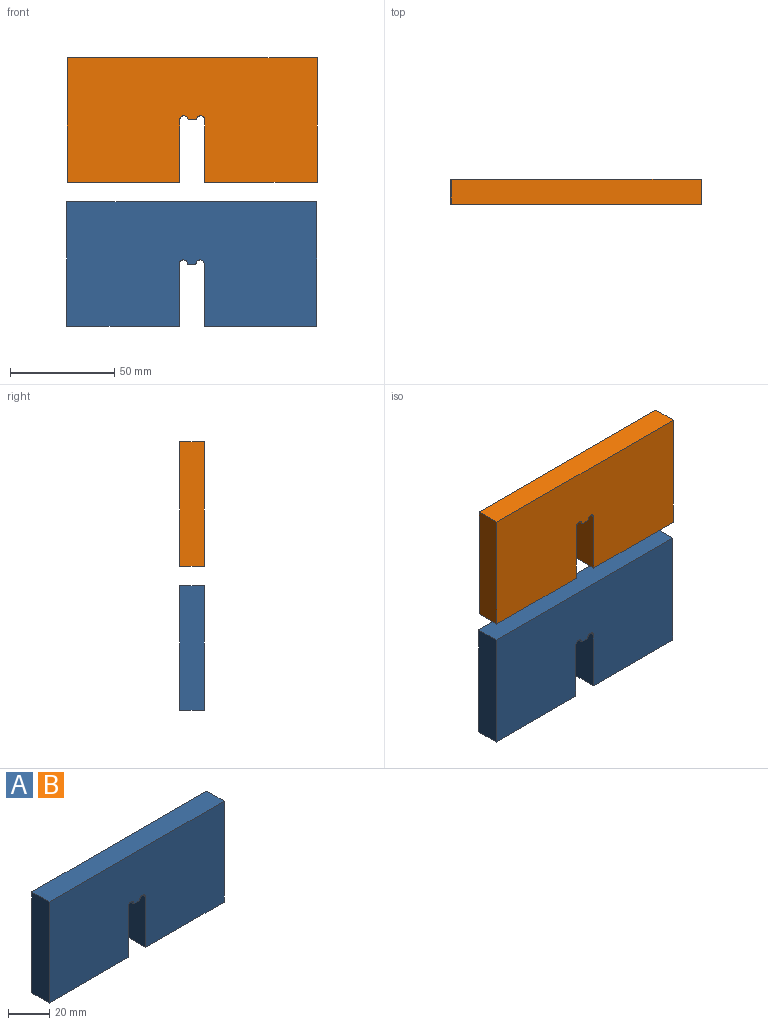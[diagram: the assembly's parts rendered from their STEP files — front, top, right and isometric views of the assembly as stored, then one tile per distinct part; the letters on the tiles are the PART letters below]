
ASSEMBLY  parts=2 mates=1
PART A: 12 faces, bbox 120x12x60 mm
  f0: plane 54x12mm, normal (0,0,-1), area 648mm2, adj f1,f9,f10,f11
  f1: plane 30x12mm, normal (1,0,0), area 360mm2, adj f0,f2,f10,f11
  f2: cylinder r=2mm len=12mm, axis (0,1,0), area 75.4mm2, adj f1,f3,f10,f11
  f3: plane 12x4mm, normal (0,0,-1), area 48mm2, adj f2,f4,f10,f11
  f4: cylinder r=2mm len=12mm, axis (0,1,0), area 75.4mm2, adj f3,f5,f10,f11
  f5: plane 30x12mm, normal (-1,0,0), area 360mm2, adj f4,f6,f10,f11
  f6: plane 54x12mm, normal (0,0,-1), area 648mm2, adj f5,f7,f10,f11
  f7: plane 60x12mm, normal (1,0,0), area 720mm2, adj f6,f8,f10,f11
  f8: plane 120x12mm, normal (0,0,1), area 1440mm2, adj f7,f9,f10,f11
  f9: plane 60x12mm, normal (-1,0,0), area 720mm2, adj f0,f8,f10,f11
  f10: plane 120x60mm, normal (0,-1,0), area 6827.4mm2, adj f0,f1,f2,f3,f4,f5,f6,f7
  f11: plane 120x60mm, normal (0,1,0), area 6827.4mm2, adj f0,f1,f2,f3,f4,f5,f6,f7
PART B: same geometry as A
PLACE A t=(-358.91,149.6,-47.98)mm
PLACE B t=(-358.66,149.6,21.25)mm fixed
MATE planar B.f10 <-> A.f10  axis (0,-1,0) through (51.91,143.6,-13.75)mm
